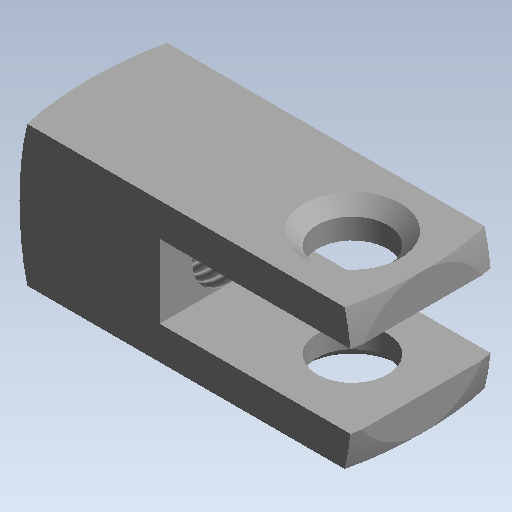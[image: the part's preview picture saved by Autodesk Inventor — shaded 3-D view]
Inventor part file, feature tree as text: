
AUTODESK INVENTOR PART (.ipt)
format: ipt  version: 2020 (Build 240168000, 168)  size: 194,048 bytes
history: native  units: mm (DEFAULTED — no unit token found)
features: other x126, sketch x7, revolve x4, extrude x2, thread x1, hole x1
ambient origin geometry x8: Origin, YZ Plane, XZ Plane, XY Plane, X Axis, Y Axis, Z Axis, Center Point
bodies: Solid1 (feature_tree)
feature tree (141):
  extrude  "Extrusion1"  Depth=12.7mm TaperAngle=0.0deg
  extrude  "Extrusion2"  Depth=10.6032mm TaperAngle=0.0deg
  revolve  "Revolution1"  Angle=360.0deg
  thread  "Thread1"  [1 undecoded]
  hole  "Hole1"  [1 undecoded]
  revolve  "Revolution2"  [1 undecoded]
  revolve  "Revolution3"  [1 undecoded]
  revolve  "Revolution4"  [1 undecoded]
  other  "dummy_XY"
  other  "dummy_YZ"
  other  "dummy_ZX"
  other  "dummy_X"
  other  "dummy_Y"
  other  "dummy_Z"
  other  "dummy_Center"
  other  "h1_XY"
  other  "h1_YZ"
  other  "h1_ZX"
  other  "h1_X"
  other  "h1_Y"
  other  "h1_Z"
  other  "h1_Center"
  other  "h2_XY"
  other  "h2_YZ"
  other  "h2_ZX"
  other  "h2_X"
  other  "h2_Y"
  other  "h2_Z"
  other  "h2_Center"
  other  "l1_XY"
  other  "l1_YZ"
  other  "l1_ZX"
  other  "l1_X"
  other  "l1_Y"
  other  "l1_Z"
  other  "l1_Center"
  other  "l11_XY"
  other  "l11_YZ"
  other  "l11_ZX"
  other  "l11_X"
  other  "l11_Y"
  other  "l11_Z"
  other  "l11_Center"
  other  "l12_XY"
  other  "l12_YZ"
  other  "l12_ZX"
  other  "l12_X"
  other  "l12_Y"
  other  "l12_Z"
  other  "l12_Center"
  other  "l2_XY"
  other  "l2_YZ"
  other  "l2_ZX"
  other  "l2_X"
  other  "l2_Y"
  other  "l2_Z"
  other  "l2_Center"
  other  "l21_XY"
  other  "l21_YZ"
  other  "l21_ZX"
  other  "l21_X"
  other  "l21_Y"
  other  "l21_Z"
  other  "l21_Center"
  other  "l22_XY"
  other  "l22_YZ"
  other  "l22_ZX"
  other  "l22_X"
  other  "l22_Y"
  other  "l22_Z"
  other  "l22_Center"
  other  "piston_rod_clevis_XY"
  other  "piston_rod_clevis_YZ"
  other  "piston_rod_clevis_ZX"
  other  "piston_rod_clevis_X"
  other  "piston_rod_clevis_Y"
  other  "piston_rod_clevis_Z"
  other  "piston_rod_clevis_Center"
  other  "rod_clevis_body_XY"
  other  "rod_clevis_body_YZ"
  other  "rod_clevis_body_ZX"
  other  "rod_clevis_body_X"
  other  "rod_clevis_body_Y"
  other  "rod_clevis_body_Z"
  other  "rod_clevis_body_Center"
  other  "th1_XY"
  other  "th1_YZ"
  other  "th1_ZX"
  other  "th1_X"
  other  "th1_Y"
  other  "th1_Z"
  other  "th1_Center"
  other  "th2_XY"
  other  "th2_YZ"
  other  "th2_ZX"
  other  "th2_X"
  other  "th2_Y"
  other  "th2_Z"
  other  "th2_Center"
  other  "to_cylinder_XY"
  other  "to_cylinder_YZ"
  other  "to_cylinder_ZX"
  other  "to_cylinder_X"
  other  "to_cylinder_Y"
  other  "to_cylinder_Z"
  other  "to_cylinder_Center"
  other  "w1_XY"
  other  "w1_YZ"
  other  "w1_ZX"
  other  "w1_X"
  other  "w1_Y"
  other  "w1_Z"
  other  "w1_Center"
  other  "w11_XY"
  other  "w11_YZ"
  other  "w11_ZX"
  other  "w11_X"
  other  "w11_Y"
  other  "w11_Z"
  other  "w11_Center"
  other  "w12_XY"
  other  "w12_YZ"
  other  "w12_ZX"
  other  "w12_X"
  other  "w12_Y"
  other  "w12_Z"
  other  "w12_Center"
  other  "w2_XY"
  other  "w2_YZ"
  other  "w2_ZX"
  other  "w2_X"
  other  "w2_Y"
  other  "w2_Z"
  other  "w2_Center"
  sketch  "Sketch_1"  dims[d0=12.7mm d1=0.0mm d2=12.7mm d3=0.0mm]
  sketch  "Sketch_2"  dims[d4=360.0deg d5=10.6032mm d6=0.0mm]
  sketch  "Sketch_3"  dims[d7=6.79196mm d8=6.0mm d9=4.0mm d10=2.0mm d11=90.0deg d12=1.524mm d13=0.0mm d14=360.0deg d15=360.0deg]
  sketch  "Sketch5"  dims[d16=360.0deg d17=0.0mm d18=0.0mm]
  sketch  "Sketch_5"
  sketch  "Sketch_9"
  sketch  "Sketch_10"
note: 5 required parameter values undecoded (feature->parameter linkage not recoverable at this tier; creation-order binding heuristic only, values carry confidence <= 0.55)
